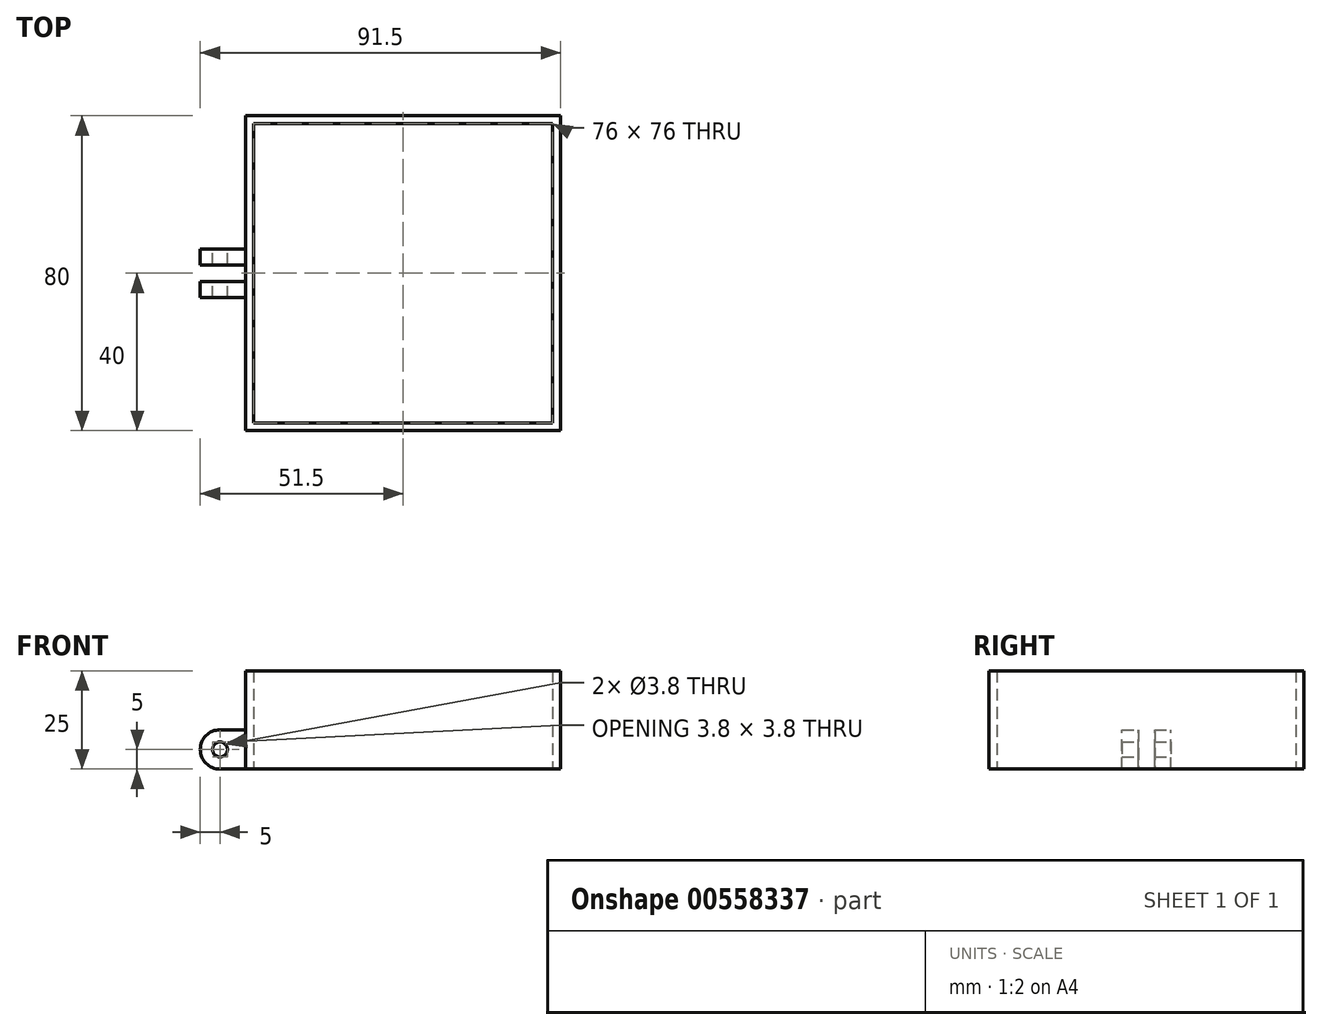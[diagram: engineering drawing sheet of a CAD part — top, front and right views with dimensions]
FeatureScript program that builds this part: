
annotation { "Feature Type Name" : "Feature", "Feature Type Description" : "" }
export const myFeature = defineFeature(function(context is Context, id is Id, definition is map)
    precondition{}
    {
        {
            var Q0;
            Q0=qCreatedBy(makeId("Top.planeOp"),FACE);
            var sketch = newSketch(context, id + "F0", { "sketchPlane" : qUnion([Q0])});
            skLineSegment(sketch, "E0.bottom", {"start": v(40, -40) * mm, "end": v(-40, -40) * mm});
            skLineSegment(sketch, "E0.top", {"start": v(40, 40) * mm, "end": v(-40, 40) * mm});
            skLineSegment(sketch, "E0.left", {"start": v(40, -40) * mm, "end": v(40, 40) * mm});
            skLineSegment(sketch, "E0.right", {"start": v(-40, -40) * mm, "end": v(-40, 40) * mm});
            skPoint(sketch, "E0.middle", {"position": v(0, 0) * mm});
            skLineSegment(sketch, "E1.0", {"start": v(-38, -38) * mm, "end": v(-38, 38) * mm});
            skLineSegment(sketch, "E1.1", {"start": v(38, -38) * mm, "end": v(-38, -38) * mm});
            skLineSegment(sketch, "E1.2", {"start": v(38, -38) * mm, "end": v(38, 38) * mm});
            skLineSegment(sketch, "E1.3", {"start": v(38, 38) * mm, "end": v(-38, 38) * mm});
            skSolve(sketch);
        }
        {
            var Q0;
            Q0=makeQuery(id+"F0.imprint","IMPRINT",FACE,{"disambiguationData":[TD([[makeQuery(id+"F0.imprint","IMPRINT",EDGE,{"derivedFrom":sQuery(id+"F0.wireOp",EDGE,"E0.bottom")}),-1.0]])]});
            extrude(context, id + "F1", {"entities" : qUnion([Q0]), "depth" : 25 * mm, "offsetDistance" : 25 * mm});
        }
        {
            var Q0;
            Q0=makeQuery(id+"F1.opExtrude","SWEPT_FACE",FACE,{"disambiguationData":[OSD([sQuery(id+"F0.wireOp",EDGE,"E0.right")])]});
            var sketch = newSketch(context, id + "F2", { "sketchPlane" : qUnion([Q0])});
            skLineSegment(sketch, "E2.bottom", {"start": v(6.2, 0) * mm, "end": v(-6.2, 0) * mm});
            skLineSegment(sketch, "E2.top", {"start": v(6.2, 10) * mm, "end": v(-6.2, 10) * mm});
            skLineSegment(sketch, "E2.left", {"start": v(6.2, 0) * mm, "end": v(6.2, 10) * mm});
            skLineSegment(sketch, "E2.right", {"start": v(-6.2, 0) * mm, "end": v(-6.2, 10) * mm});
            skPoint(sketch, "E2.middle", {"position": v(0, 5) * mm});
            skSolve(sketch);
        }
        {
            var Q0;
            Q0=makeQuery(id+"F2.imprint","IMPRINT",FACE,{"disambiguationData":[TD([[makeQuery(id+"F2.imprint","IMPRINT",EDGE,{"derivedFrom":sQuery(id+"F2.wireOp",EDGE,"E2.bottom")}),-1.0]])]});
            extrude(context, id + "F3", {"entities" : qUnion([Q0]), "operationType" : NewBodyOperationType.ADD, "depth" : 11.5 * mm, "offsetDistance" : 25 * mm});
        }
        {
            var Q0;
            Q0=makeQuery(id+"F3.opExtrude","CAP_EDGE",EDGE,{"disambiguationData":[OSD([sQuery(id+"F2.wireOp",EDGE,"E2.top")])],"isStart":false});
            var Q1;
            Q1=makeQuery(id+"F3.opExtrude","CAP_EDGE",EDGE,{"disambiguationData":[OSD([sQuery(id+"F2.wireOp",EDGE,"E2.bottom")])],"isStart":false});
            fillet(context, id + "F4", {"entities" : qUnion([Q0, Q1]), "radius" : 5 * mm, "tangentPropagation" : true, "allowEdgeOverflow" : false});
        }
        {
            var Q0;
            Q0=makeQuery(id+"F3.opExtrude","SWEPT_FACE",FACE,{"disambiguationData":[OSD([sQuery(id+"F2.wireOp",EDGE,"E2.right")])]});
            var sketch = newSketch(context, id + "F5", { "sketchPlane" : qUnion([Q0])});
            skCircle(sketch, "E3", {"center": v(46.5, 5) * mm, "radius": 1.9 * mm});
            skSolve(sketch);
        }
        {
            var Q0;
            Q0=makeQuery(id+"F5.imprint","IMPRINT",FACE,{"disambiguationData":[TD([[makeQuery(id+"F5.imprint","IMPRINT",EDGE,{"derivedFrom":sQuery(id+"F5.wireOp",EDGE,"E3")}),1.0]])]});
            extrude(context, id + "F6", {"entities" : qUnion([Q0]), "operationType" : NewBodyOperationType.REMOVE, "oppositeDirection" : true, "depth" : 25 * mm, "offsetDistance" : 25 * mm});
        }
        {
            var Q0;
            Q0=makeQuery(id+"F3.opExtrude","SWEPT_FACE",FACE,{"disambiguationData":[OSD([sQuery(id+"F2.wireOp",EDGE,"E2.top")])]});
            var sketch = newSketch(context, id + "F7", { "sketchPlane" : qUnion([Q0])});
            skLineSegment(sketch, "E4.bottom", {"start": v(-51.5, -2.1) * mm, "end": v(-40, -2.1) * mm});
            skLineSegment(sketch, "E4.top", {"start": v(-51.5, 2.1) * mm, "end": v(-40, 2.1) * mm});
            skLineSegment(sketch, "E4.left", {"start": v(-51.5, -2.1) * mm, "end": v(-51.5, 2.1) * mm});
            skLineSegment(sketch, "E4.right", {"start": v(-40, -2.1) * mm, "end": v(-40, 2.1) * mm});
            skPoint(sketch, "E4.middle", {"position": v(-45.75, 0) * mm});
            skSolve(sketch);
        }
        {
            var Q0;
            {var subQ0=sQuery(id+"F7.wireOp",EDGE,"E4.right");Q0=makeQuery(id+"F7.imprint","IMPRINT",FACE,{"disambiguationData":[TD([[makeQuery(id+"F7.imprint","IMPRINT",EDGE,{"derivedFrom":subQ0}),1.0]])]});}
            var Q1;
            {var subQ0=sQuery(id+"F7.wireOp",EDGE,"E4.left");Q1=makeQuery(id+"F7.imprint","IMPRINT",FACE,{"disambiguationData":[TD([[makeQuery(id+"F7.imprint","IMPRINT",EDGE,{"derivedFrom":subQ0}),-1.0]])]});}
            extrude(context, id + "F8", {"entities" : qUnion([Q0, Q1]), "operationType" : NewBodyOperationType.REMOVE, "oppositeDirection" : true, "depth" : 25 * mm, "offsetDistance" : 25 * mm});
        }
    });
